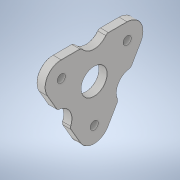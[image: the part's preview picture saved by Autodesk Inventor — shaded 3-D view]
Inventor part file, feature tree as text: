
AUTODESK INVENTOR PART (.ipt)
format: ipt  version: 2021 (Build 250183000, 183)  size: 240,640 bytes
history: native  units: in
note: dims shown in document units (in); Inventor stores cm internally (conversion verified against a paired STEP export)
features: extrude x2, sketch x2, fillet x1, chamfer x1
ambient origin geometry x8: Origin, YZ Plane, XZ Plane, XY Plane, X Axis, Y Axis, Z Axis, Center Point
bodies: Solid1 (feature_tree)
feature tree (6):
  extrude  "Extrusion1"  Depth=0.125in TaperAngle=360.0deg
  fillet  "Fillet2"  Radius=0.125in
  extrude  "Extrusion3"  Depth=0.125in
  chamfer  "Chamfer4"  Distance=0.3153in
  sketch  "Sketch1"  dims[d4=0.325in d5=0.0in d26=1.1811in d28=360.0deg d30=0.125in]
  sketch  "Sketch5"  dims[d34=1.25in d35=1.135in d36=0.3153in d37=1.25in d38=1.25in d39=60.0deg d40=60.0deg d41=0.2903in d42=2.1897in d43=2.1897in d44=0.0in d45=1.6222in d46=0.0in d47=2.4668in d48=3.1515in d49=0.0in d50=3.1515in d51=0.625in d52=0.625in d53=0.9375in d54=3.1515in d55=1.363in d56=1.363in d57=1.6222in d58=0.0in d59=1.6222in d60=2.4668in d61=2.4668in d62=0.0in d63=2.4668in d64=1.6222in d65=2.839in d66=3.1515in d67=0.0in d68=3.1515in d69=0.9375in d70=1.0in d71=1.0in d72=0.0in d73=0.01in d74=0.125in d75=45.0deg]
